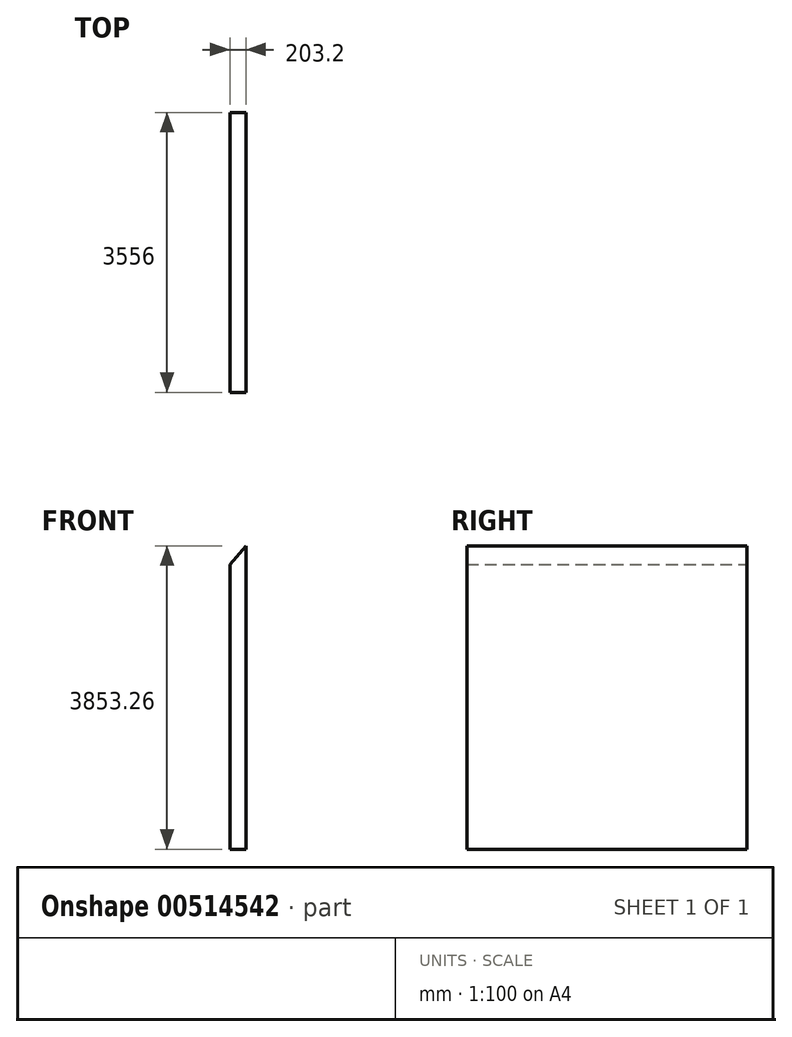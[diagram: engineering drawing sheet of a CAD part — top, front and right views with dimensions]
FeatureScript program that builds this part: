
annotation { "Feature Type Name" : "Feature", "Feature Type Description" : "" }
export const myFeature = defineFeature(function(context is Context, id is Id, definition is map)
    precondition{}
    {
        {
            var Q0;
            Q0=qCreatedBy(makeId("Right.planeOp"),FACE);
            var sketch = newSketch(context, id + "F0", { "sketchPlane" : qUnion([Q0])});
            skLineSegment(sketch, "E0.bottom", {"start": v(-1778, 2353.82) * mm, "end": v(1778, 2353.82) * mm});
            skLineSegment(sketch, "E0.top", {"start": v(-1778, -2353.82) * mm, "end": v(1778, -2353.82) * mm});
            skLineSegment(sketch, "E0.left", {"start": v(-1778, 2353.82) * mm, "end": v(-1778, -2353.82) * mm});
            skLineSegment(sketch, "E0.right", {"start": v(1778, 2353.82) * mm, "end": v(1778, -2353.82) * mm});
            skPoint(sketch, "E0.middle", {"position": v(0, 0) * mm});
            skSolve(sketch);
        }
        {
            var Q0;
            Q0=makeQuery(id+"F0.imprint","IMPRINT",FACE,{"disambiguationData":[TD([[makeQuery(id+"F0.imprint","IMPRINT",EDGE,{"derivedFrom":sQuery(id+"F0.wireOp",EDGE,"E0.bottom")}),-1.0]])]});
            extrude(context, id + "F1", {"entities" : qUnion([Q0]), "depth" : 203.2 * mm, "offsetDistance" : 25.4 * mm});
        }
        {
            var Q0;
            Q0=makeQuery(id+"F1.opExtrude","SWEPT_FACE",FACE,{"disambiguationData":[OSD([sQuery(id+"F0.wireOp",EDGE,"E0.left")])]});
            var sketch = newSketch(context, id + "F2", { "sketchPlane" : qUnion([Q0])});
            skLineSegment(sketch, "E1", {"start": v(203.2, -2353.82) * mm, "end": v(203.2, 1265.68) * mm});
            skLineSegment(sketch, "E2", {"start": v(203.2, 1265.68) * mm, "end": v(0, 1499.44) * mm});
            skLineSegment(sketch, "E3.0", {"start": v(203.2, 2353.82) * mm, "end": v(203.2, -2353.82) * mm});
            skLineSegment(sketch, "E3.1", {"start": v(0, 2353.82) * mm, "end": v(0, -2353.82) * mm});
            skLineSegment(sketch, "E3.2", {"start": v(203.2, 2353.82) * mm, "end": v(0, 2353.82) * mm});
            skSolve(sketch);
        }
        {
            var Q0;
            {var subQ0=sQuery(id+"F2.wireOp",EDGE,"E2");Q0=makeQuery(id+"F2.imprint","IMPRINT",FACE,{"disambiguationData":[TD([[makeQuery(id+"F2.imprint","IMPRINT",EDGE,{"derivedFrom":subQ0}),-1.0]])]});}
            extrude(context, id + "F3", {"entities" : qUnion([Q0]), "operationType" : NewBodyOperationType.REMOVE, "oppositeDirection" : true, "depth" : 3556 * mm, "offsetDistance" : 25.4 * mm});
        }
        {
            var Q0;
            Q0=makeQuery(id+"F1.opExtrude","CAP_FACE",FACE,{"disambiguationData":[OSD([sQuery(id+"F0.wireOp",EDGE,"E0.bottom"),sQuery(id+"F0.wireOp",EDGE,"E0.top"),sQuery(id+"F0.wireOp",EDGE,"E0.left"),sQuery(id+"F0.wireOp",EDGE,"E0.right")])],"isStart":true});
            var sketch = newSketch(context, id + "F4", { "sketchPlane" : qUnion([Q0])});
            skLineSegment(sketch, "E4", {"start": v(0, 0) * mm, "end": v(0, -1429.95) * mm});
            skSolve(sketch);
        }
        {
            var Q0;
            Q0=makeQuery(id+"F1.opExtrude","SWEPT_BODY",BODY,{"disambiguationData":[OSD([sQuery(id+"F0.wireOp",EDGE,"E0.bottom"),sQuery(id+"F0.wireOp",EDGE,"E0.top"),sQuery(id+"F0.wireOp",EDGE,"E0.left"),sQuery(id+"F0.wireOp",EDGE,"E0.right")])]});
            var Q1;
            Q1=sQuery(id+"F4.wireOp",EDGE,"E4");
            transform(context, id + "F5", {"entities" : qUnion([Q0]), "transformType" : TransformType.ROTATION, "transformAxis" : qUnion([Q1]), "angle" : 180 * degree, "makeCopy" : false});
        }
    });
